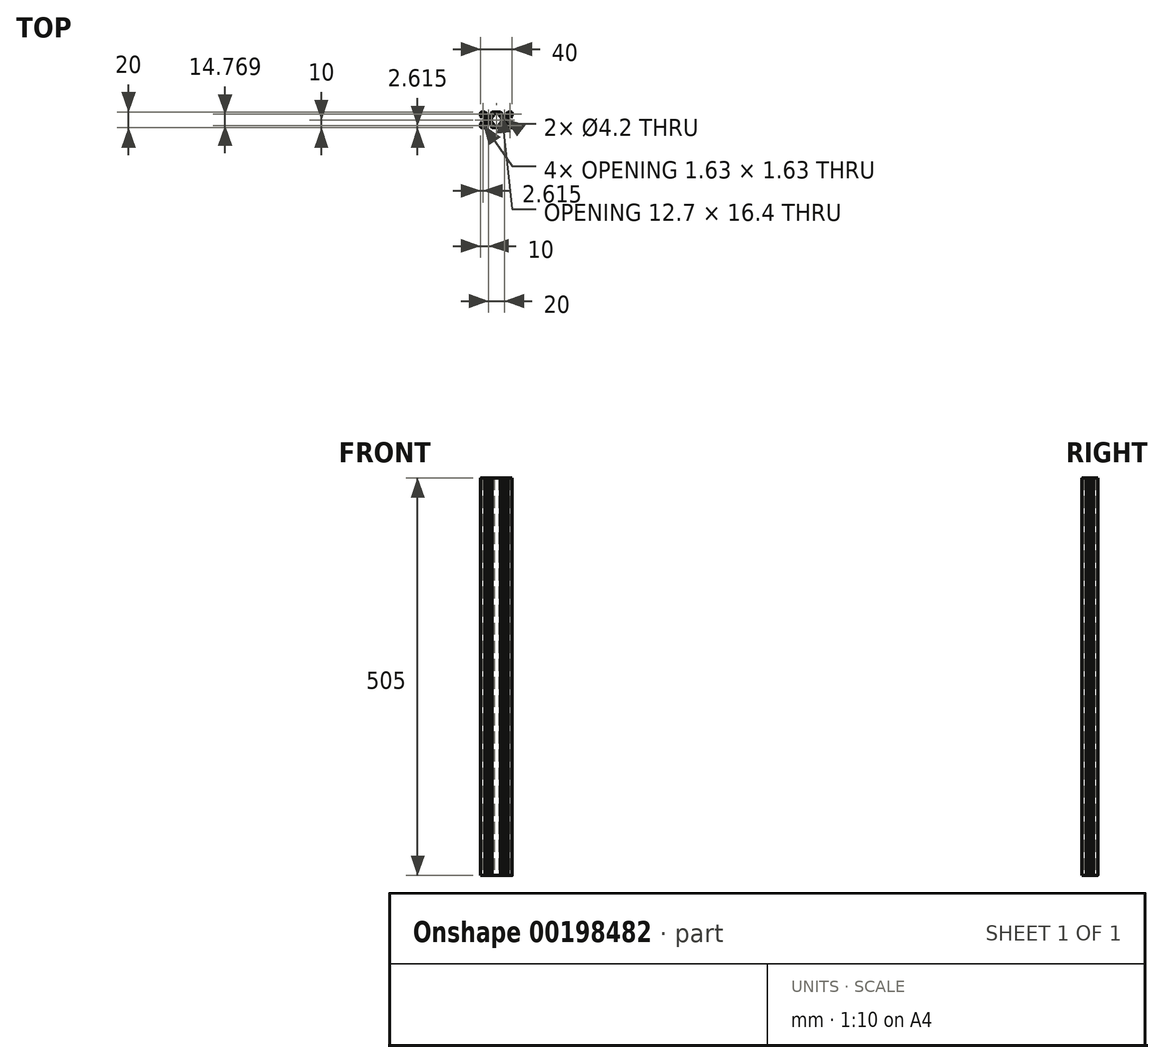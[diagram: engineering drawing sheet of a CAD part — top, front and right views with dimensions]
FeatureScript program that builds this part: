
annotation { "Feature Type Name" : "Feature", "Feature Type Description" : "" }
export const myFeature = defineFeature(function(context is Context, id is Id, definition is map)
    precondition{}
    {
        {
            var Q0;
            Q0=qCreatedBy(makeId("Top.planeOp"),FACE);
            var sketch = newSketch(context, id + "F0", { "sketchPlane" : qUnion([Q0])});
            skLineSegment(sketch, "E0", {"start": v(8.5, -10) * mm, "end": v(4.64, -10) * mm});
            skLineSegment(sketch, "E1", {"start": v(-10, -8.5) * mm, "end": v(-10, -4.64) * mm});
            skLineSegment(sketch, "E2", {"start": v(-8.5, 10) * mm, "end": v(-4.64, 10) * mm});
            skLineSegment(sketch, "E3.0", {"start": v(-5.5, 8.2) * mm, "end": v(-2.84, 8.2) * mm});
            skLineSegment(sketch, "E3.1", {"start": v(-8.2, -5.5) * mm, "end": v(-8.2, -2.84) * mm});
            skLineSegment(sketch, "E3.2", {"start": v(5.5, -8.2) * mm, "end": v(2.84, -8.2) * mm});
            skLineSegment(sketch, "E4.trimOffspring", {"start": v(4.64, 10) * mm, "end": v(8.5, 10) * mm});
            skLineSegment(sketch, "E5", {"start": v(-2.84, 8.2) * mm, "end": v(-4.64, 10) * mm});
            skLineSegment(sketch, "E6.trimOffspring", {"start": v(2.84, 8.2) * mm, "end": v(5.5, 8.2) * mm});
            skLineSegment(sketch, "E7.MirrorCS", {"start": v(2.84, 8.2) * mm, "end": v(4.64, 10) * mm});
            skLineSegment(sketch, "E8.MirrorCS", {"start": v(2.84, -8.2) * mm, "end": v(4.64, -10) * mm});
            skLineSegment(sketch, "E9.MirrorCS", {"start": v(-2.84, -8.2) * mm, "end": v(-4.64, -10) * mm});
            skLineSegment(sketch, "E10.trimOffspring", {"start": v(-2.84, -8.2) * mm, "end": v(-5.5, -8.2) * mm});
            skLineSegment(sketch, "E11.trimOffspring", {"start": v(-4.64, -10) * mm, "end": v(-8.5, -10) * mm});
            skLineSegment(sketch, "E12", {"start": v(-8.2, 2.84) * mm, "end": v(-10, 4.64) * mm});
            skLineSegment(sketch, "E13", {"start": v(-8.2, -2.84) * mm, "end": v(-10, -4.64) * mm});
            skLineSegment(sketch, "E14.trimOffspring", {"start": v(-10, 4.64) * mm, "end": v(-10, 8.5) * mm});
            skLineSegment(sketch, "E15.trimOffspring", {"start": v(-8.2, 2.84) * mm, "end": v(-8.2, 5.5) * mm});
            skCircle(sketch, "E16", {"center": v(0, 0) * mm, "radius": 2.1 * mm});
            skLineSegment(sketch, "E17", {"start": v(-6.56, 5.5) * mm, "end": v(-3.9, 2.84) * mm});
            skLineSegment(sketch, "E18", {"start": v(-5.5, 6.56) * mm, "end": v(-2.84, 3.9) * mm});
            skLineSegment(sketch, "E19", {"start": v(-5.5, 6.56) * mm, "end": v(-5.5, 8.2) * mm});
            skLineSegment(sketch, "E20", {"start": v(-6.56, 5.5) * mm, "end": v(-8.2, 5.5) * mm});
            skLineSegment(sketch, "E21", {"start": v(6.56, 5.5) * mm, "end": v(3.9, 2.84) * mm});
            skLineSegment(sketch, "E22", {"start": v(5.5, 6.56) * mm, "end": v(2.84, 3.9) * mm});
            skLineSegment(sketch, "E23", {"start": v(-6.56, -5.5) * mm, "end": v(-8.2, -5.5) * mm});
            skLineSegment(sketch, "E24", {"start": v(-5.5, -6.56) * mm, "end": v(-5.5, -8.2) * mm});
            skLineSegment(sketch, "E25", {"start": v(5.5, 6.56) * mm, "end": v(5.5, 8.2) * mm});
            skLineSegment(sketch, "E26", {"start": v(5.5, -6.56) * mm, "end": v(5.5, -8.2) * mm});
            skLineSegment(sketch, "E27.trimOffspring", {"start": v(2.84, -3.9) * mm, "end": v(5.5, -6.56) * mm});
            skLineSegment(sketch, "E28.trimOffspring", {"start": v(-2.84, -3.9) * mm, "end": v(-5.5, -6.56) * mm});
            skLineSegment(sketch, "E29.trimOffspring", {"start": v(-3.9, -2.84) * mm, "end": v(-6.56, -5.5) * mm});
            skLineSegment(sketch, "E30.trimOffspring", {"start": v(3.9, -2.84) * mm, "end": v(6.56, -5.5) * mm});
            skLineSegment(sketch, "E31", {"start": v(-3.9, -2.84) * mm, "end": v(-3.9, -0.25) * mm});
            skLineSegment(sketch, "E32", {"start": v(-2.84, 3.9) * mm, "end": v(-0.25, 3.9) * mm});
            skLineSegment(sketch, "E33", {"start": v(-2.84, -3.9) * mm, "end": v(-0.25, -3.9) * mm});
            skLineSegment(sketch, "E34", {"start": v(3.9, 2.84) * mm, "end": v(3.9, 0.25) * mm});
            skLineSegment(sketch, "E35", {"start": v(-8.2, 6.57) * mm, "end": v(-8.2, 8.2) * mm});
            skLineSegment(sketch, "E36", {"start": v(-6.57, 8.2) * mm, "end": v(-8.2, 8.2) * mm});
            skLineSegment(sketch, "E37", {"start": v(-8.2, 6.57) * mm, "end": v(-7.63, 6.57) * mm});
            skLineSegment(sketch, "E38", {"start": v(-6.57, 8.2) * mm, "end": v(-6.57, 7.63) * mm});
            skLineSegment(sketch, "E39", {"start": v(-7.63, 6.57) * mm, "end": v(-6.57, 7.63) * mm});
            skLineSegment(sketch, "E40.MirrorCS", {"start": v(-6.57, -8.2) * mm, "end": v(-8.2, -8.2) * mm});
            skLineSegment(sketch, "E41.MirrorCS", {"start": v(-8.2, -6.57) * mm, "end": v(-7.63, -6.57) * mm});
            skLineSegment(sketch, "E42.MirrorCS", {"start": v(-8.2, -6.57) * mm, "end": v(-8.2, -8.2) * mm});
            skLineSegment(sketch, "E43.MirrorCS", {"start": v(-7.63, -6.57) * mm, "end": v(-6.57, -7.63) * mm});
            skLineSegment(sketch, "E44.MirrorCS", {"start": v(-6.57, -8.2) * mm, "end": v(-6.57, -7.63) * mm});
            skArc(sketch, "E45.filletArc", {"start": v(-8.5, 10) * mm, "mid": v(-9.56, 9.56) * mm, "end": v(-10, 8.5) * mm});
            skPoint(sketch, "E46.visualSharp", {"position": v(10, 10) * mm});
            skArc(sketch, "E47.filletArc", {"start": v(-10, -8.5) * mm, "mid": v(-9.56, -9.56) * mm, "end": v(-8.5, -10) * mm});
            skLineSegment(sketch, "E48", {"start": v(-3.65, 0) * mm, "end": v(-3.9, 0.25) * mm});
            skLineSegment(sketch, "E49.MirrorCS", {"start": v(-3.65, 0) * mm, "end": v(-3.9, -0.25) * mm});
            skLineSegment(sketch, "E50.trimOffspring", {"start": v(-3.9, 0.25) * mm, "end": v(-3.9, 2.84) * mm});
            skLineSegment(sketch, "E51.MirrorCS", {"start": v(3.65, 0) * mm, "end": v(3.9, 0.25) * mm});
            skLineSegment(sketch, "E52.MirrorCS", {"start": v(3.65, 0) * mm, "end": v(3.9, -0.25) * mm});
            skLineSegment(sketch, "E53", {"start": v(0, -3.65) * mm, "end": v(0.25, -3.9) * mm});
            skLineSegment(sketch, "E54.MirrorCS", {"start": v(0, -3.65) * mm, "end": v(-0.25, -3.9) * mm});
            skLineSegment(sketch, "E55.trimOffspring", {"start": v(0.25, -3.9) * mm, "end": v(2.84, -3.9) * mm});
            skLineSegment(sketch, "E56.trimOffspring", {"start": v(3.9, -0.25) * mm, "end": v(3.9, -2.84) * mm});
            skLineSegment(sketch, "E57.MirrorCS", {"start": v(0, 3.65) * mm, "end": v(-0.25, 3.9) * mm});
            skLineSegment(sketch, "E58.MirrorCS", {"start": v(0, 3.65) * mm, "end": v(0.25, 3.9) * mm});
            skLineSegment(sketch, "E59.trimOffspring", {"start": v(0.25, 3.9) * mm, "end": v(2.84, 3.9) * mm});
            skLineSegment(sketch, "E60.MirrorCS", {"start": v(20, -3.65) * mm, "end": v(19.75, -3.9) * mm});
            skLineSegment(sketch, "E61.MirrorCS", {"start": v(20, -3.65) * mm, "end": v(20.25, -3.9) * mm});
            skLineSegment(sketch, "E62.MirrorCS", {"start": v(23.65, 0) * mm, "end": v(23.9, 0.25) * mm});
            skLineSegment(sketch, "E63.MirrorCS", {"start": v(23.65, 0) * mm, "end": v(23.9, -0.25) * mm});
            skLineSegment(sketch, "E64.MirrorCS", {"start": v(16.35, 0) * mm, "end": v(16.1, 0.25) * mm});
            skLineSegment(sketch, "E65.MirrorCS", {"start": v(16.35, 0) * mm, "end": v(16.1, -0.25) * mm});
            skLineSegment(sketch, "E66.MirrorCS", {"start": v(28.2, -6.57) * mm, "end": v(27.63, -6.57) * mm});
            skLineSegment(sketch, "E67.MirrorCS", {"start": v(20, 3.65) * mm, "end": v(20.25, 3.9) * mm});
            skLineSegment(sketch, "E68.MirrorCS", {"start": v(20, 3.65) * mm, "end": v(19.75, 3.9) * mm});
            skLineSegment(sketch, "E69.MirrorCS", {"start": v(28.2, 6.57) * mm, "end": v(27.63, 6.57) * mm});
            skLineSegment(sketch, "E70.MirrorCS", {"start": v(26.57, -8.2) * mm, "end": v(26.57, -7.63) * mm});
            skLineSegment(sketch, "E71.MirrorCS", {"start": v(26.57, 8.2) * mm, "end": v(26.57, 7.63) * mm});
            skLineSegment(sketch, "E72.MirrorCS", {"start": v(28.2, 2.84) * mm, "end": v(28.2, 5.5) * mm});
            skLineSegment(sketch, "E73.MirrorCS", {"start": v(14.5, -6.56) * mm, "end": v(14.5, -8.2) * mm});
            skArc(sketch, "E74.MirrorCS", {"start": v(30, -8.5) * mm, "mid": v(29.56, -9.56) * mm, "end": v(28.5, -10) * mm});
            skLineSegment(sketch, "E75.MirrorCS", {"start": v(17.16, -3.9) * mm, "end": v(14.5, -6.56) * mm});
            skLineSegment(sketch, "E76.MirrorCS", {"start": v(22.84, -3.9) * mm, "end": v(25.5, -6.56) * mm});
            skPoint(sketch, "E77.MirrorP", {"position": v(10, -10) * mm});
            skLineSegment(sketch, "E78.MirrorCS", {"start": v(23.9, -2.84) * mm, "end": v(26.56, -5.5) * mm});
            skLineSegment(sketch, "E79.MirrorCS", {"start": v(23.9, 0.25) * mm, "end": v(23.9, 2.84) * mm});
            skLineSegment(sketch, "E80.MirrorCS", {"start": v(16.1, -2.84) * mm, "end": v(13.44, -5.5) * mm});
            skCircle(sketch, "E81.MirrorC", {"center": v(20, 0) * mm, "radius": 2.1 * mm});
            skLineSegment(sketch, "E82.MirrorCS", {"start": v(23.9, -2.84) * mm, "end": v(23.9, -0.25) * mm});
            skLineSegment(sketch, "E83.MirrorCS", {"start": v(26.56, 5.5) * mm, "end": v(23.9, 2.84) * mm});
            skLineSegment(sketch, "E84.MirrorCS", {"start": v(22.84, 3.9) * mm, "end": v(20.25, 3.9) * mm});
            skLineSegment(sketch, "E85.MirrorCS", {"start": v(25.5, 6.56) * mm, "end": v(22.84, 3.9) * mm});
            skLineSegment(sketch, "E86.MirrorCS", {"start": v(22.84, -3.9) * mm, "end": v(20.25, -3.9) * mm});
            skLineSegment(sketch, "E87.MirrorCS", {"start": v(25.5, 6.56) * mm, "end": v(25.5, 8.2) * mm});
            skLineSegment(sketch, "E88.MirrorCS", {"start": v(16.1, -0.25) * mm, "end": v(16.1, -2.84) * mm});
            skLineSegment(sketch, "E89.MirrorCS", {"start": v(28.2, 6.57) * mm, "end": v(28.2, 8.2) * mm});
            skLineSegment(sketch, "E90.MirrorCS", {"start": v(13.44, 5.5) * mm, "end": v(16.1, 2.84) * mm});
            skLineSegment(sketch, "E91.MirrorCS", {"start": v(26.57, -8.2) * mm, "end": v(28.2, -8.2) * mm});
            skLineSegment(sketch, "E92.MirrorCS", {"start": v(16.1, 2.84) * mm, "end": v(16.1, 0.25) * mm});
            skLineSegment(sketch, "E93.MirrorCS", {"start": v(26.56, 5.5) * mm, "end": v(28.2, 5.5) * mm});
            skLineSegment(sketch, "E94.MirrorCS", {"start": v(19.75, -3.9) * mm, "end": v(17.16, -3.9) * mm});
            skLineSegment(sketch, "E95.MirrorCS", {"start": v(28.2, -6.57) * mm, "end": v(28.2, -8.2) * mm});
            skLineSegment(sketch, "E96.MirrorCS", {"start": v(26.57, 8.2) * mm, "end": v(28.2, 8.2) * mm});
            skLineSegment(sketch, "E97.MirrorCS", {"start": v(14.5, 6.56) * mm, "end": v(17.16, 3.9) * mm});
            skLineSegment(sketch, "E98.MirrorCS", {"start": v(27.63, -6.57) * mm, "end": v(26.57, -7.63) * mm});
            skLineSegment(sketch, "E99.MirrorCS", {"start": v(26.56, -5.5) * mm, "end": v(28.2, -5.5) * mm});
            skLineSegment(sketch, "E100.MirrorCS", {"start": v(22.84, -8.2) * mm, "end": v(24.64, -10) * mm});
            skLineSegment(sketch, "E101.MirrorCS", {"start": v(22.84, -8.2) * mm, "end": v(25.5, -8.2) * mm});
            skLineSegment(sketch, "E102.MirrorCS", {"start": v(24.64, -10) * mm, "end": v(28.5, -10) * mm});
            skLineSegment(sketch, "E103.MirrorCS", {"start": v(11.5, -10) * mm, "end": v(15.36, -10) * mm});
            skLineSegment(sketch, "E104.MirrorCS", {"start": v(30, -8.5) * mm, "end": v(30, -4.64) * mm});
            skLineSegment(sketch, "E105.MirrorCS", {"start": v(28.5, 10) * mm, "end": v(24.64, 10) * mm});
            skLineSegment(sketch, "E106.MirrorCS", {"start": v(25.5, 8.2) * mm, "end": v(22.84, 8.2) * mm});
            skLineSegment(sketch, "E107.MirrorCS", {"start": v(28.2, -5.5) * mm, "end": v(28.2, -2.84) * mm});
            skLineSegment(sketch, "E108.MirrorCS", {"start": v(14.5, -8.2) * mm, "end": v(17.16, -8.2) * mm});
            skLineSegment(sketch, "E109.MirrorCS", {"start": v(15.36, 10) * mm, "end": v(11.5, 10) * mm});
            skLineSegment(sketch, "E110.MirrorCS", {"start": v(22.84, 8.2) * mm, "end": v(24.64, 10) * mm});
            skLineSegment(sketch, "E111.MirrorCS", {"start": v(17.16, 8.2) * mm, "end": v(14.5, 8.2) * mm});
            skLineSegment(sketch, "E112.MirrorCS", {"start": v(17.16, 8.2) * mm, "end": v(15.36, 10) * mm});
            skLineSegment(sketch, "E113.MirrorCS", {"start": v(17.16, -8.2) * mm, "end": v(15.36, -10) * mm});
            skLineSegment(sketch, "E114.MirrorCS", {"start": v(28.2, 2.84) * mm, "end": v(30, 4.64) * mm});
            skLineSegment(sketch, "E115.MirrorCS", {"start": v(19.75, 3.9) * mm, "end": v(17.16, 3.9) * mm});
            skLineSegment(sketch, "E116.MirrorCS", {"start": v(25.5, -6.56) * mm, "end": v(25.5, -8.2) * mm});
            skLineSegment(sketch, "E117.MirrorCS", {"start": v(28.2, -2.84) * mm, "end": v(30, -4.64) * mm});
            skArc(sketch, "E118.MirrorCS", {"start": v(28.5, 10) * mm, "mid": v(29.56, 9.56) * mm, "end": v(30, 8.5) * mm});
            skLineSegment(sketch, "E119.MirrorCS", {"start": v(27.63, 6.57) * mm, "end": v(26.57, 7.63) * mm});
            skLineSegment(sketch, "E120.MirrorCS", {"start": v(14.5, 6.56) * mm, "end": v(14.5, 8.2) * mm});
            skLineSegment(sketch, "E121.MirrorCS", {"start": v(30, 4.64) * mm, "end": v(30, 8.5) * mm});
            skLineSegment(sketch, "E122", {"start": v(8.5, 10) * mm, "end": v(11.5, 10) * mm});
            skLineSegment(sketch, "E123", {"start": v(8.5, -10) * mm, "end": v(11.5, -10) * mm});
            skLineSegment(sketch, "E124", {"start": v(7, 8.2) * mm, "end": v(13, 8.2) * mm});
            skLineSegment(sketch, "E125", {"start": v(7, -8.2) * mm, "end": v(7, -5.94) * mm});
            skLineSegment(sketch, "E126", {"start": v(3.9, -2.84) * mm, "end": v(7, -5.94) * mm});
            skLineSegment(sketch, "E127", {"start": v(13, -8.2) * mm, "end": v(13, -5.94) * mm});
            skLineSegment(sketch, "E128", {"start": v(16.1, -2.84) * mm, "end": v(13, -5.94) * mm});
            skLineSegment(sketch, "E129", {"start": v(7, -8.2) * mm, "end": v(13, -8.2) * mm});
            skLineSegment(sketch, "E130", {"start": v(16.1, 2.84) * mm, "end": v(13, 5.94) * mm});
            skLineSegment(sketch, "E131", {"start": v(3.9, 2.84) * mm, "end": v(6.56, 5.5) * mm});
            skLineSegment(sketch, "E132", {"start": v(6.56, 5.5) * mm, "end": v(7, 5.94) * mm});
            skLineSegment(sketch, "E133.trimOffspring", {"start": v(7, 5.94) * mm, "end": v(7, 8.2) * mm});
            skLineSegment(sketch, "E134", {"start": v(13, 5.94) * mm, "end": v(13, 8.2) * mm});
            skSolve(sketch);
        }
        {
            var Q0;
            Q0=makeQuery(id+"F0.imprint","IMPRINT",FACE,{"disambiguationData":[TD([[makeQuery(id+"F0.imprint","IMPRINT",EDGE,{"derivedFrom":sQuery(id+"F0.wireOp",EDGE,"E0")}),-1.0]])]});
            extrude(context, id + "F1", {"entities" : qUnion([Q0]), "depth" : 505 * mm});
        }
    });
